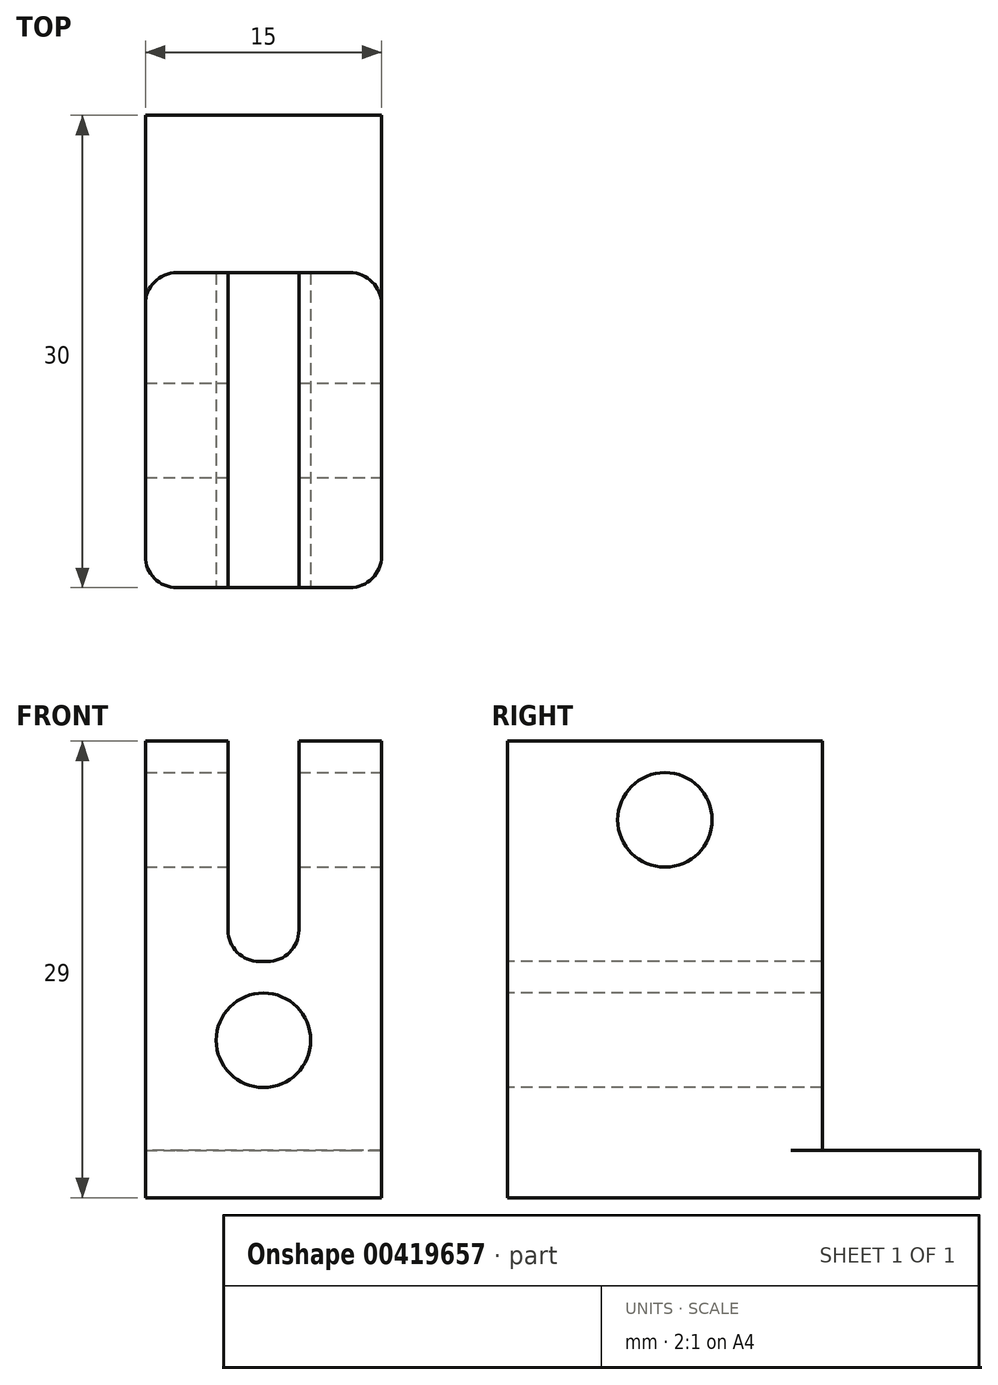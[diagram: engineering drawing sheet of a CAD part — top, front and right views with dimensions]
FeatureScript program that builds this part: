
annotation { "Feature Type Name" : "Feature", "Feature Type Description" : "" }
export const myFeature = defineFeature(function(context is Context, id is Id, definition is map)
    precondition{}
    {
        {
            var Q0;
            Q0=qCreatedBy(makeId("Top.planeOp"),FACE);
            var sketch = newSketch(context, id + "F0", { "sketchPlane" : qUnion([Q0])});
            skLineSegment(sketch, "E0.top", {"start": v(7.5, -10) * mm, "end": v(-7.5, -10) * mm});
            skLineSegment(sketch, "E0.left", {"start": v(7.5, 10) * mm, "end": v(7.5, -10) * mm});
            skLineSegment(sketch, "E0.right", {"start": v(-7.5, 10) * mm, "end": v(-7.5, -10) * mm});
            skPoint(sketch, "E0.middle", {"position": v(0, 0) * mm});
            skLineSegment(sketch, "E1", {"start": v(-7.5, 10) * mm, "end": v(7.5, 10) * mm});
            skSolve(sketch);
        }
        {
            var Q0;
            Q0=qSketchRegion(id+"F0",true);
            extrude(context, id + "F1", {"entities" : qUnion([Q0]), "depth" : 26 * mm});
        }
        {
            var Q0;
            Q0=qCreatedBy(makeId("Front.planeOp"),FACE);
            var sketch = newSketch(context, id + "F2", { "sketchPlane" : qUnion([Q0])});
            skCircle(sketch, "E2", {"center": v(0, 7) * mm, "radius": 3 * mm});
            skPoint(sketch, "E3", {"position": v(0, 4) * mm});
            skSolve(sketch);
        }
        {
            var Q0;
            Q0=qSketchRegion(id+"F2",true);
            extrude(context, id + "F3", {"entities" : qUnion([Q0]), "operationType" : NewBodyOperationType.REMOVE, "endBound" : BoundingType.THROUGH_ALL, "oppositeDirection" : true, "depth" : 25 * mm, "hasSecondDirection" : true, "secondDirectionBound" : SecondDirectionBoundingType.THROUGH_ALL, "secondDirectionOppositeDirection" : false, "secondDirectionDepth" : 25 * mm});
        }
        {
            var Q0;
            Q0=qCreatedBy(makeId("Right.planeOp"),FACE);
            var sketch = newSketch(context, id + "F4", { "sketchPlane" : qUnion([Q0])});
            skCircle(sketch, "E4", {"center": v(0, 21) * mm, "radius": 3 * mm});
            skPoint(sketch, "E5", {"position": v(0, 24) * mm});
            skSolve(sketch);
        }
        {
            var Q0;
            Q0=qSketchRegion(id+"F4",true);
            extrude(context, id + "F5", {"entities" : qUnion([Q0]), "operationType" : NewBodyOperationType.REMOVE, "endBound" : BoundingType.THROUGH_ALL, "oppositeDirection" : true, "depth" : 25 * mm, "hasSecondDirection" : true, "secondDirectionBound" : SecondDirectionBoundingType.THROUGH_ALL, "secondDirectionOppositeDirection" : false, "secondDirectionDepth" : 25 * mm});
        }
        {
            var Q0;
            Q0=qCreatedBy(makeId("Front.planeOp"),FACE);
            var sketch = newSketch(context, id + "F6", { "sketchPlane" : qUnion([Q0])});
            skLineSegment(sketch, "E6.bottom", {"start": v(2.25, 26) * mm, "end": v(-2.25, 26) * mm});
            skLineSegment(sketch, "E6.top", {"start": v(2.25, 12) * mm, "end": v(-2.25, 12) * mm});
            skLineSegment(sketch, "E6.left", {"start": v(2.25, 26) * mm, "end": v(2.25, 12) * mm});
            skLineSegment(sketch, "E6.right", {"start": v(-2.25, 26) * mm, "end": v(-2.25, 12) * mm});
            skLineSegment(sketch, "E7", {"start": v(0, 0) * mm, "end": v(0, 12) * mm, "construction": true});
            skLineSegment(sketch, "E8.0", {"start": v(7.5, 24) * mm, "end": v(7.5, 18) * mm, "construction": true});
            skSolve(sketch);
        }
        {
            var Q0;
            Q0=qSketchRegion(id+"F6",true);
            extrude(context, id + "F7", {"entities" : qUnion([Q0]), "operationType" : NewBodyOperationType.REMOVE, "endBound" : BoundingType.THROUGH_ALL, "oppositeDirection" : true, "depth" : 25 * mm, "hasSecondDirection" : true, "secondDirectionBound" : SecondDirectionBoundingType.THROUGH_ALL, "secondDirectionOppositeDirection" : false, "secondDirectionDepth" : 25 * mm});
        }
        {
            var Q0;
            Q0=makeQuery(id+"F1.opExtrude","CAP_FACE",FACE,{"disambiguationData":[OSD([sQuery(id+"F0.wireOp",EDGE,"E0.bottom"),sQuery(id+"F0.wireOp",EDGE,"E0.top"),sQuery(id+"F0.wireOp",EDGE,"E0.left"),sQuery(id+"F0.wireOp",EDGE,"E0.right")])],"isStart":true});
            var sketch = newSketch(context, id + "F8", { "sketchPlane" : qUnion([Q0])});
            skLineSegment(sketch, "E9.bottom", {"start": v(7.5, 10) * mm, "end": v(-7.5, 10) * mm});
            skLineSegment(sketch, "E9.top", {"start": v(7.5, -20) * mm, "end": v(-7.5, -20) * mm});
            skLineSegment(sketch, "E9.left", {"start": v(7.5, 10) * mm, "end": v(7.5, -20) * mm});
            skLineSegment(sketch, "E9.right", {"start": v(-7.5, 10) * mm, "end": v(-7.5, -20) * mm});
            skSolve(sketch);
        }
        {
            var Q0;
            Q0=qSketchRegion(id+"F8",true);
            extrude(context, id + "F9", {"entities" : qUnion([Q0]), "operationType" : NewBodyOperationType.ADD, "depth" : 3 * mm});
        }
        {
            var Q0;
            Q0=makeQuery(id+"F1.opExtrude","SWEPT_EDGE",EDGE,{"disambiguationData":[OSD([sQuery(id+"F0.wireOp",EDGE,"E0.bottom"),sQuery(id+"F0.wireOp",EDGE,"E0.left")])]});
            var Q1;
            Q1=makeQuery(id+"F1.opExtrude","SWEPT_EDGE",EDGE,{"disambiguationData":[OSD([sQuery(id+"F0.wireOp",EDGE,"E0.bottom"),sQuery(id+"F0.wireOp",EDGE,"E0.right")])]});
            var Q2;
            Q2=makeQuery(id+"F1.opExtrude","SWEPT_EDGE",EDGE,{"disambiguationData":[OSD([sQuery(id+"F0.wireOp",EDGE,"E0.top"),sQuery(id+"F0.wireOp",EDGE,"E0.left")])]});
            var Q3;
            Q3=makeQuery(id+"F1.opExtrude","SWEPT_EDGE",EDGE,{"disambiguationData":[OSD([sQuery(id+"F0.wireOp",EDGE,"E0.top"),sQuery(id+"F0.wireOp",EDGE,"E0.right")])]});
            var Q4;
            Q4=makeQuery(id+"F1.opExtrude","CAP_EDGE",EDGE,{"disambiguationData":[OSD([sQuery(id+"F0.wireOp",EDGE,"E0.bottom")])],"isStart":true});
            fillet(context, id + "F10", {"entities" : qUnion([Q0, Q1, Q2, Q3, Q4]), "radius" : 2 * mm, "tangentPropagation" : true, "allowEdgeOverflow" : false});
        }
        {
            var Q0;
            Q0=makeQuery(id+"F7.boolean.opBoolean","COPY",EDGE,{"derivedFrom":makeQuery(id+"F7.opExtrude","SWEPT_EDGE",EDGE,{"disambiguationData":[OSD([sQuery(id+"F6.wireOp",EDGE,"E6.top"),sQuery(id+"F6.wireOp",EDGE,"E6.left")])]})});
            var Q1;
            Q1=makeQuery(id+"F7.boolean.opBoolean","COPY",EDGE,{"derivedFrom":makeQuery(id+"F7.opExtrude","SWEPT_EDGE",EDGE,{"disambiguationData":[OSD([sQuery(id+"F6.wireOp",EDGE,"E6.top"),sQuery(id+"F6.wireOp",EDGE,"E6.right")])]})});
            fillet(context, id + "F11", {"entities" : qUnion([Q0, Q1]), "radius" : 2 * mm, "tangentPropagation" : true, "allowEdgeOverflow" : false});
        }
    });
